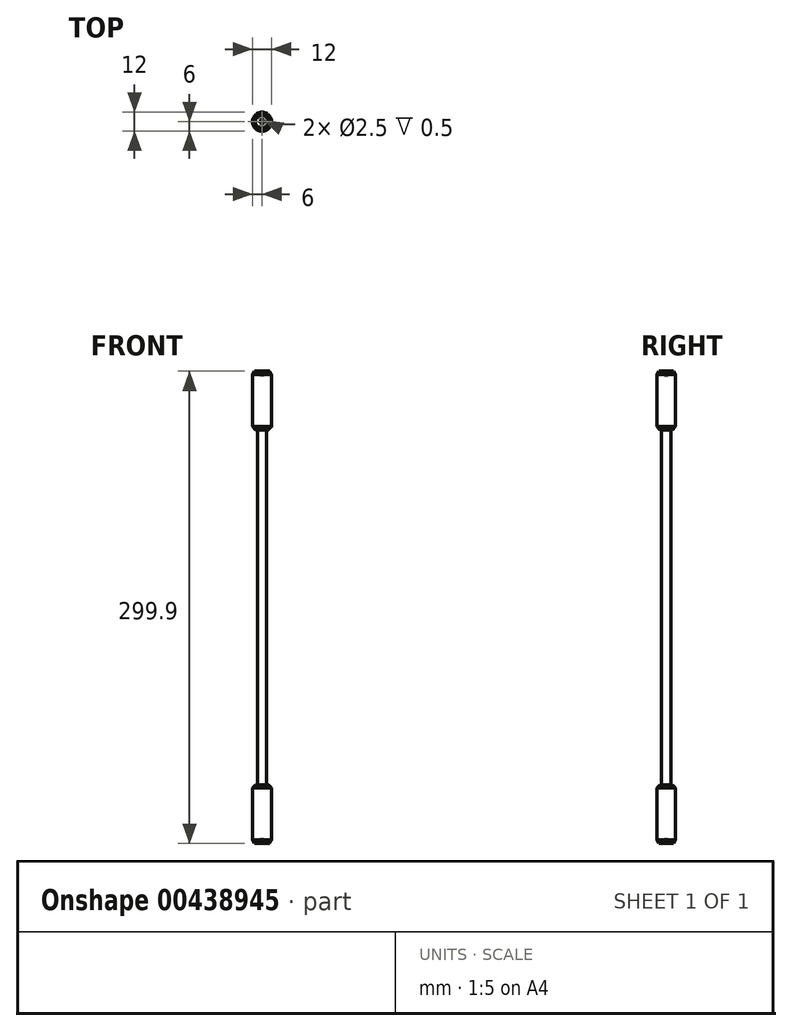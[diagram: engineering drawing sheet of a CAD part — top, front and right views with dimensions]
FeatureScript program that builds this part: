
annotation { "Feature Type Name" : "Feature", "Feature Type Description" : "" }
export const myFeature = defineFeature(function(context is Context, id is Id, definition is map)
    precondition{}
    {
        {
            var Q0;
            Q0=qCreatedBy(makeId("Front.planeOp"),FACE);
            var sketch = newSketch(context, id + "F0", { "sketchPlane" : qUnion([Q0])});
            skLineSegment(sketch, "E0", {"start": v(0, 254.6) * mm, "end": v(0, -61.97) * mm, "construction": true});
            skLineSegment(sketch, "E1.bottom", {"start": v(0, 0) * mm, "end": v(-2.92, 0) * mm});
            skLineSegment(sketch, "E1.top", {"start": v(0, 112.7) * mm, "end": v(-2.92, 112.7) * mm});
            skLineSegment(sketch, "E1.left", {"start": v(0, 0) * mm, "end": v(0, 112.7) * mm});
            skLineSegment(sketch, "E1.right", {"start": v(-2.92, 0) * mm, "end": v(-2.92, 112.7) * mm});
            skLineSegment(sketch, "E2.bottom", {"start": v(-2.92, 112.7) * mm, "end": v(-4, 112.7) * mm});
            skLineSegment(sketch, "E2.top", {"start": v(-4.22, 149.95) * mm, "end": v(-4.75, 149.95) * mm});
            skLineSegment(sketch, "E2.left", {"start": v(0, 112.7) * mm, "end": v(0, 147.35) * mm});
            skLineSegment(sketch, "E2.right", {"start": v(-6, 114.7) * mm, "end": v(-6, 147.78) * mm});
            skLineSegment(sketch, "E3", {"start": v(-6, 147.78) * mm, "end": v(-4.75, 149.95) * mm});
            skLineSegment(sketch, "E4", {"start": v(-4, 112.7) * mm, "end": v(-6, 114.7) * mm});
            skArc(sketch, "E5", {"start": v(-4.22, 149.95) * mm, "mid": v(-3, 148.42) * mm, "end": v(-1.25, 147.52) * mm});
            skLineSegment(sketch, "E6.top", {"start": v(-1.25, 147.02) * mm, "end": v(0, 147.02) * mm});
            skLineSegment(sketch, "E6.left", {"start": v(-1.25, 147.52) * mm, "end": v(-1.25, 147.02) * mm});
            skLineSegment(sketch, "E6.right", {"start": v(0, 147.47) * mm, "end": v(0, 147.02) * mm});
            skSolve(sketch);
        }
        {
            var Q0;
            Q0 = qSketchRegion(id + "F0", true);
            var Q1;
            Q1=sQuery(id+"F0.wireOp",EDGE,"E0");
            revolve(context, id + "F1", {"entities" : qUnion([Q0]), "axis" : qUnion([Q1]), "revolveType" : RevolveType.FULL});
        }
        {
            var Q0;
            Q0=makeQuery(id+"F1.opRevolve","SWEPT_BODY",BODY,{"disambiguationData":[OSD([sQuery(id+"F0.wireOp",EDGE,"E1.bottom"),sQuery(id+"F0.wireOp",EDGE,"E1.left"),sQuery(id+"F0.wireOp",EDGE,"E1.right"),sQuery(id+"F0.wireOp",EDGE,"E2.bottom"),sQuery(id+"F0.wireOp",EDGE,"E2.top"),sQuery(id+"F0.wireOp",EDGE,"E2.left"),sQuery(id+"F0.wireOp",EDGE,"E2.right"),sQuery(id+"F0.wireOp",EDGE,"E3"),sQuery(id+"F0.wireOp",EDGE,"E4"),sQuery(id+"F0.wireOp",EDGE,"E5")])]});
            var Q1;
            Q1=qCreatedBy(makeId("Top.planeOp"),FACE);
            mirror(context, id + "F2", {"operationType" : NewBodyOperationType.ADD, "entities" : qUnion([Q0]), "mirrorPlane" : qUnion([Q1])});
        }
    });
